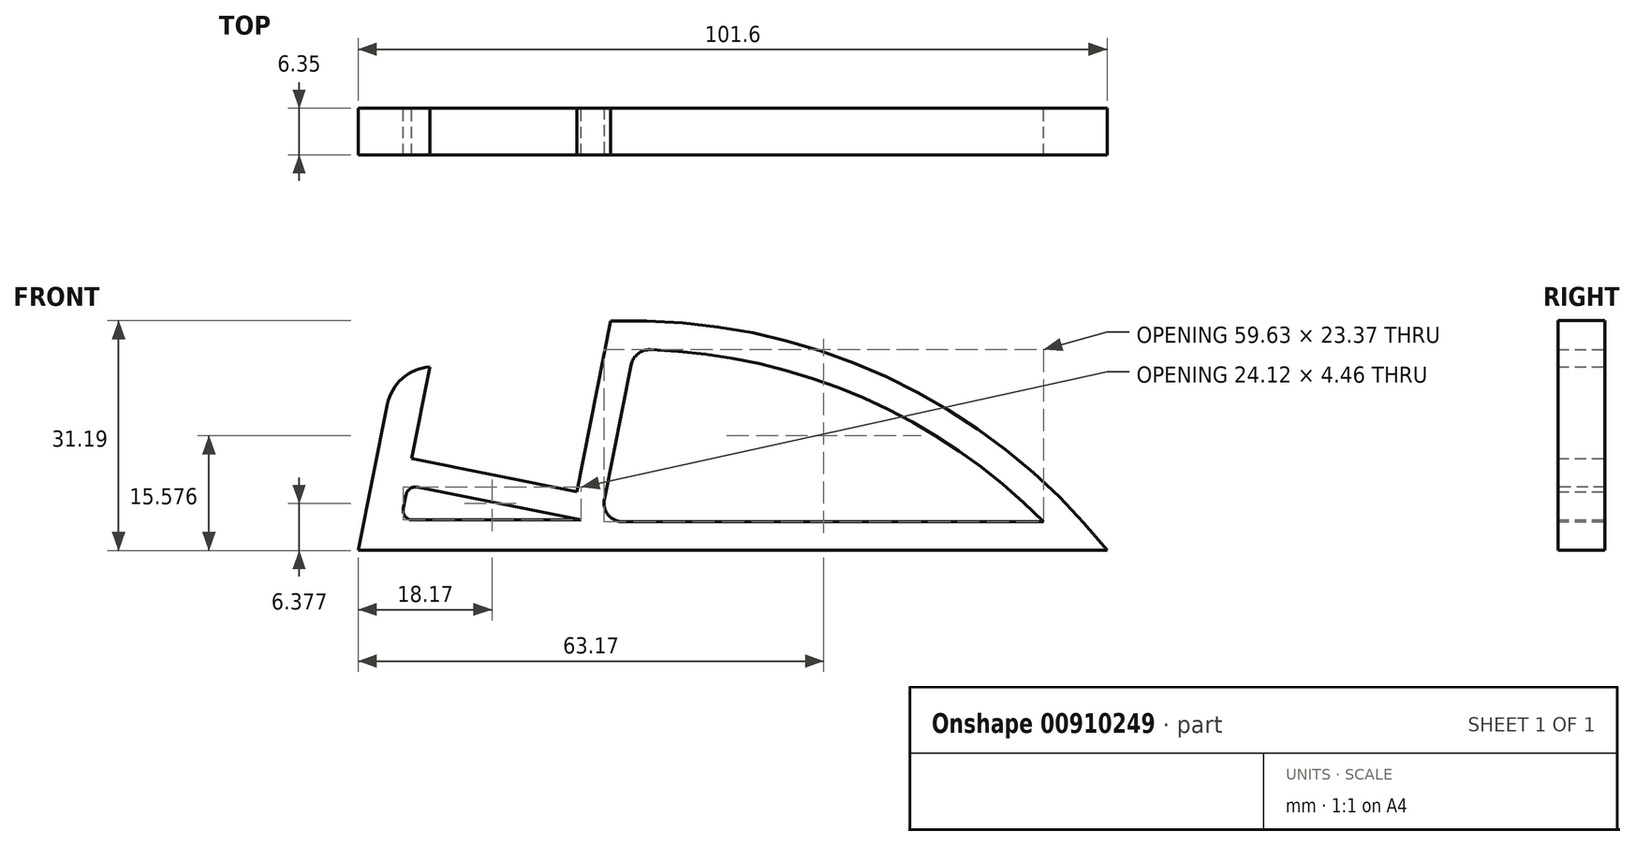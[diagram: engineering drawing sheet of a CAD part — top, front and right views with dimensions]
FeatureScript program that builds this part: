
annotation { "Feature Type Name" : "Feature", "Feature Type Description" : "" }
export const myFeature = defineFeature(function(context is Context, id is Id, definition is map)
    precondition{}
    {
        {
            var Q0;
            Q0=qCreatedBy(makeId("Front.planeOp"),FACE);
            var sketch = newSketch(context, id + "F0", { "sketchPlane" : qUnion([Q0])});
            skLineSegment(sketch, "E0", {"start": v(-42.17, 26.28) * mm, "end": v(-48.4, -4.86) * mm});
            skLineSegment(sketch, "E1", {"start": v(-48.4, -4.86) * mm, "end": v(53.2, -4.86) * mm});
            skArc(sketch, "E2", {"start": v(53.2, -4.86) * mm, "mid": v(23.25, 18.73) * mm, "end": v(-14.11, 26.28) * mm});
            skLineSegment(sketch, "E3", {"start": v(-41.16, 7.6) * mm, "end": v(-18.74, 3.12) * mm});
            skLineSegment(sketch, "E4", {"start": v(-14.11, 26.28) * mm, "end": v(-18.74, 3.12) * mm});
            skArc(sketch, "E5.0", {"start": v(44.6, -0.97) * mm, "mid": v(19.18, 16.28) * mm, "end": v(-10.92, 22.44) * mm});
            skLineSegment(sketch, "E5.1", {"start": v(-15.6, -0.97) * mm, "end": v(44.6, -0.97) * mm});
            skLineSegment(sketch, "E5.2", {"start": v(-10.92, 22.44) * mm, "end": v(-15.6, -0.97) * mm});
            skLineSegment(sketch, "E6.0", {"start": v(-18.16, -0.72) * mm, "end": v(-41.62, 3.97) * mm});
            skLineSegment(sketch, "E6.1", {"start": v(-18.16, -0.72) * mm, "end": v(-42.56, -0.72) * mm});
            skLineSegment(sketch, "E6.2", {"start": v(-41.62, 3.97) * mm, "end": v(-42.56, -0.72) * mm});
            skLineSegment(sketch, "E7", {"start": v(-41.16, 7.6) * mm, "end": v(-38.67, 20.05) * mm});
            skLineSegment(sketch, "E8", {"start": v(-38.67, 20.05) * mm, "end": v(-45.16, 20.05) * mm});
            skSolve(sketch);
        }
        {
            var Q0;
            Q0=makeQuery(id+"F0.imprint","IMPRINT",FACE,{"disambiguationData":[TD([[makeQuery(id+"F0.imprint","IMPRINT",EDGE,{"derivedFrom":sQuery(id+"F0.wireOp",EDGE,"E0")}),1.0]])]});
            extrude(context, id + "F1", {"entities" : qUnion([Q0]), "depth" : 76.2 * mm, "offsetDistance" : 25.4 * mm});
        }
        {
            var Q0;
            Q0=makeQuery(id+"F1.opExtrude","SWEPT_EDGE",EDGE,{"disambiguationData":[OSD([sQuery(id+"F0.wireOp",EDGE,"E5.0"),sQuery(id+"F0.wireOp",EDGE,"E5.2")])]});
            var Q1;
            Q1=makeQuery(id+"F1.opExtrude","SWEPT_EDGE",EDGE,{"disambiguationData":[OSD([sQuery(id+"F0.wireOp",EDGE,"E5.1"),sQuery(id+"F0.wireOp",EDGE,"E5.2")])]});
            fillet(context, id + "F2", {"entities" : qUnion([Q0, Q1]), "radius" : 2.54 * mm, "tangentPropagation" : true, "allowEdgeOverflow" : false});
        }
        {
            var Q0;
            Q0=makeQuery(id+"F1.opExtrude","SWEPT_EDGE",EDGE,{"disambiguationData":[OSD([sQuery(id+"F0.wireOp",EDGE,"E6.0"),sQuery(id+"F0.wireOp",EDGE,"E6.2")])]});
            var Q1;
            Q1=makeQuery(id+"F1.opExtrude","SWEPT_EDGE",EDGE,{"disambiguationData":[OSD([sQuery(id+"F0.wireOp",EDGE,"E6.1"),sQuery(id+"F0.wireOp",EDGE,"E6.2")])]});
            fillet(context, id + "F3", {"entities" : qUnion([Q0, Q1]), "radius" : 1.27 * mm, "tangentPropagation" : true, "allowEdgeOverflow" : false});
        }
        {
            var Q0;
            Q0=makeQuery(id+"F1.opExtrude","SWEPT_EDGE",EDGE,{"disambiguationData":[OSD([sQuery(id+"F0.wireOp",EDGE,"E0"),sQuery(id+"F0.wireOp",EDGE,"E8")])]});
            fillet(context, id + "F4", {"entities" : qUnion([Q0]), "radius" : 6.35 * mm, "tangentPropagation" : true, "allowEdgeOverflow" : false});
        }
        {
            var Q0;
            Q0=makeQuery(id+"F1.opExtrude","CAP_FACE",FACE,{"disambiguationData":[OSD([sQuery(id+"F0.wireOp",EDGE,"E0"),sQuery(id+"F0.wireOp",EDGE,"E1"),sQuery(id+"F0.wireOp",EDGE,"E2"),sQuery(id+"F0.wireOp",EDGE,"E3"),sQuery(id+"F0.wireOp",EDGE,"E4"),sQuery(id+"F0.wireOp",EDGE,"E5.0"),sQuery(id+"F0.wireOp",EDGE,"E5.1"),sQuery(id+"F0.wireOp",EDGE,"E5.2"),sQuery(id+"F0.wireOp",EDGE,"E6.0"),sQuery(id+"F0.wireOp",EDGE,"E6.1"),sQuery(id+"F0.wireOp",EDGE,"E6.2"),sQuery(id+"F0.wireOp",EDGE,"E7"),sQuery(id+"F0.wireOp",EDGE,"E8")])],"isStart":false});
            extrude(context, id + "F5", {"entities" : qUnion([Q0]), "operationType" : NewBodyOperationType.REMOVE, "oppositeDirection" : true, "depth" : 69.85 * mm, "offsetDistance" : 25.4 * mm});
        }
    });
